# Revit family: Basin-Undercounter-American_Standard-Studio-0426_Series
name_source: partatom
category: Plumbing Fixtures
revit_build: Autodesk Revit 2014 (Build: 20130308_1515(x64)
units: mm (PartAtom-declared; Revit-internal decimal feet)

## types (1)
- 0426.000
    ADA Compliant = Yes
    Assembly Code = D2010310
    Basin Shape = Oval
    Bowl Length = 13 1/2"
    Bowl Width = 13 1/2"
    CW Connection = Yes
    CWFU = 1.5
    Cold Water Connection Diameter = 1/2"
    Cold Water Connection Height = 10 3/4"
    Cold Water Connection Radius = 1/4"
    Cold Water Connection Width = 4"
    Default Elevation = 34"
    Description = Cadet Universal Access Countertop Sink'
    HW Connection = Yes
    HWFU = 1.5
    Height = 6 3/4"
    Hot Water Connection Diameter = 1"
    Hot Water Connection Height = 10 3/4"
    Hot Water Connection Radius = 1/4"
    Hot Water Connection Width = 4"
    Installation Type = Countertop
    Length = 16"
    Manufacturer = American Standard
    Material = Vitreous China-American Standard-020-White
    Model = 0426.000
    Price = Prices may vary. Please consult Manufacturer Representative for most up-to-date price list.
    Product Documentation Link = http://www.americanstandard.ca
    Product Page URL = http://www.americanstandard.ca
    Revised Date = 25/02/2016
    URL = http://www.americanstandard.ca
    Vent Connection = No
    WFU = 2
    Waste Connection = Yes
    Waste Connection Diameter = 1 1/4"
    Waste Connection Height = 13"
    Waste Connection Radius = 5/8"
    Width = 16"

## geometry (parser evidence)
native form markers: Sweep x1
no freeform markers — native parametric forms only
